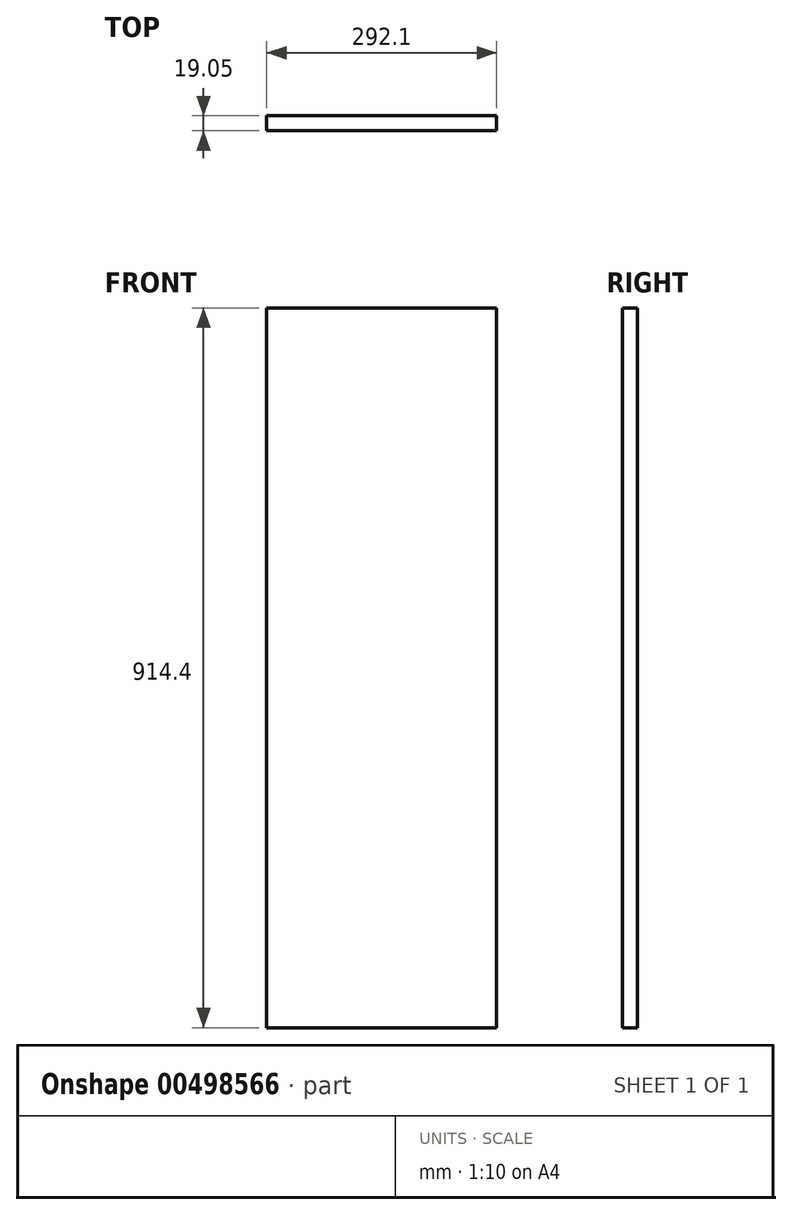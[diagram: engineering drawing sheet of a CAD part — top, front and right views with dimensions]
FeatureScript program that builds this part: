
annotation { "Feature Type Name" : "Feature", "Feature Type Description" : "" }
export const myFeature = defineFeature(function(context is Context, id is Id, definition is map)
    precondition{}
    {
        {
            var Q0;
            Q0=qCreatedBy(makeId("Front.planeOp"),FACE);
            var sketch = newSketch(context, id + "F0", { "sketchPlane" : qUnion([Q0])});
            skLineSegment(sketch, "E0.bottom", {"start": v(0, 0) * mm, "end": v(292.1, 0) * mm});
            skLineSegment(sketch, "E0.top", {"start": v(0, 914.4) * mm, "end": v(292.1, 914.4) * mm});
            skLineSegment(sketch, "E0.left", {"start": v(0, 0) * mm, "end": v(0, 914.4) * mm});
            skLineSegment(sketch, "E0.right", {"start": v(292.1, 0) * mm, "end": v(292.1, 914.4) * mm});
            skSolve(sketch);
        }
        {
            var Q0;
            Q0 = qSketchRegion(id + "F0", true);
            extrude(context, id + "F1", {"entities" : qUnion([Q0]), "depth" : 19.05 * mm, "offsetDistance" : 25.4 * mm});
        }
    });
